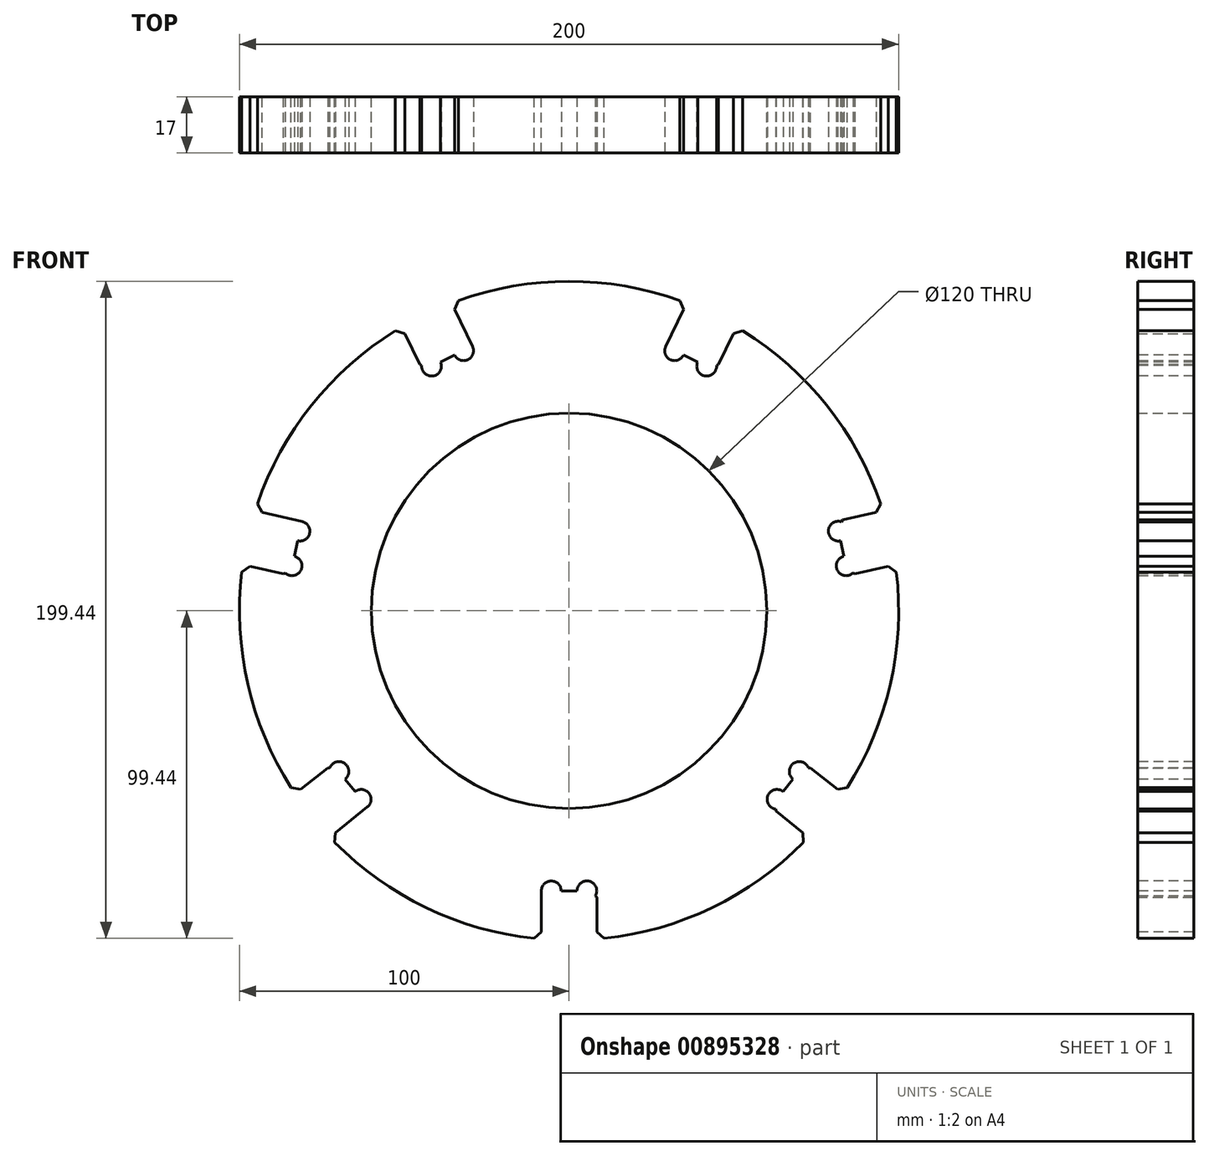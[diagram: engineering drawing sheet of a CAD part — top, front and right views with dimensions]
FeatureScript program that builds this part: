
annotation { "Feature Type Name" : "Feature", "Feature Type Description" : "" }
export const myFeature = defineFeature(function(context is Context, id is Id, definition is map)
    precondition{}
    {
        {
            var Q0;
            Q0=qCreatedBy(makeId("Front.planeOp"),FACE);
            var sketch = newSketch(context, id + "F0", { "sketchPlane" : qUnion([Q0])});
            skArc(sketch, "E0", {"start": v(8.4, -99.65) * mm, "mid": v(43.39, -90.1) * mm, "end": v(72.67, -68.7) * mm});
            skCircle(sketch, "E1", {"center": v(0, 0) * mm, "radius": 60 * mm});
            skLineSegment(sketch, "E2", {"start": v(0, 0) * mm, "end": v(0, -60) * mm});
            skLineSegment(sketch, "E3.0", {"start": v(-8.4, 0) * mm, "end": v(-8.4, -59.4) * mm});
            skLineSegment(sketch, "E4.0", {"start": v(8.4, 0) * mm, "end": v(8.4, -59.4) * mm});
            skLineSegment(sketch, "E5", {"start": v(0, -85) * mm, "end": v(8.4, -85) * mm});
            skLineSegment(sketch, "E6", {"start": v(8.4, -85) * mm, "end": v(-8.4, -85) * mm});
            skLineSegment(sketch, "E7.trimOffspring", {"start": v(-8.4, -85) * mm, "end": v(-8.4, -100) * mm});
            skLineSegment(sketch, "E8.trimOffspring", {"start": v(8.4, -85) * mm, "end": v(8.4, -100) * mm});
            skLineSegment(sketch, "E9.1.0", {"start": v(71.7, -46.43) * mm, "end": v(83.42, -55.78) * mm});
            skLineSegment(sketch, "E9.1.1", {"start": v(71.7, -46.43) * mm, "end": v(61.22, -59.56) * mm});
            skLineSegment(sketch, "E9.1.2", {"start": v(61.22, -59.56) * mm, "end": v(72.95, -68.92) * mm});
            skLineSegment(sketch, "E9.1.3", {"start": v(66.46, -53) * mm, "end": v(71.7, -46.43) * mm});
            skLineSegment(sketch, "E9.2.0", {"start": v(81, 27.1) * mm, "end": v(95.62, 30.44) * mm});
            skLineSegment(sketch, "E9.2.1", {"start": v(81, 27.1) * mm, "end": v(84.74, 10.72) * mm});
            skLineSegment(sketch, "E9.2.2", {"start": v(84.74, 10.72) * mm, "end": v(99.36, 14.06) * mm});
            skLineSegment(sketch, "E9.2.3", {"start": v(82.87, 18.91) * mm, "end": v(81, 27.1) * mm});
            skLineSegment(sketch, "E9.3.0", {"start": v(29.31, 80.23) * mm, "end": v(35.82, 93.74) * mm});
            skLineSegment(sketch, "E9.3.1", {"start": v(29.31, 80.23) * mm, "end": v(44.45, 72.94) * mm});
            skLineSegment(sketch, "E9.3.2", {"start": v(44.45, 72.94) * mm, "end": v(50.96, 86.45) * mm});
            skLineSegment(sketch, "E9.3.3", {"start": v(36.88, 76.58) * mm, "end": v(29.31, 80.23) * mm});
            skLineSegment(sketch, "E9.4.0", {"start": v(-44.45, 72.94) * mm, "end": v(-50.96, 86.45) * mm});
            skLineSegment(sketch, "E9.4.1", {"start": v(-44.45, 72.94) * mm, "end": v(-29.31, 80.23) * mm});
            skLineSegment(sketch, "E9.4.2", {"start": v(-29.31, 80.23) * mm, "end": v(-35.82, 93.74) * mm});
            skLineSegment(sketch, "E9.4.3", {"start": v(-36.88, 76.58) * mm, "end": v(-44.45, 72.94) * mm});
            skLineSegment(sketch, "E9.5.0", {"start": v(-84.74, 10.72) * mm, "end": v(-99.36, 14.06) * mm});
            skLineSegment(sketch, "E9.5.1", {"start": v(-84.74, 10.72) * mm, "end": v(-81, 27.1) * mm});
            skLineSegment(sketch, "E9.5.2", {"start": v(-81, 27.1) * mm, "end": v(-95.62, 30.44) * mm});
            skLineSegment(sketch, "E9.5.3", {"start": v(-82.87, 18.91) * mm, "end": v(-84.74, 10.72) * mm});
            skLineSegment(sketch, "E9.6.0", {"start": v(-61.22, -59.56) * mm, "end": v(-72.95, -68.92) * mm});
            skLineSegment(sketch, "E9.6.1", {"start": v(-61.22, -59.56) * mm, "end": v(-71.7, -46.43) * mm});
            skLineSegment(sketch, "E9.6.2", {"start": v(-71.7, -46.43) * mm, "end": v(-83.42, -55.78) * mm});
            skLineSegment(sketch, "E9.6.3", {"start": v(-66.46, -53) * mm, "end": v(-61.22, -59.56) * mm});
            skArc(sketch, "E10.trimOffspring", {"start": v(-99.02, 13.98) * mm, "mid": v(-99.9, -4.49) * mm, "end": v(-97.37, -22.8) * mm});
            skArc(sketch, "E11.trimOffspring", {"start": v(-92.17, -38.78) * mm, "mid": v(-88.06, -47.39) * mm, "end": v(-83.14, -55.56) * mm});
            skArc(sketch, "E12.trimOffspring", {"start": v(-72.67, -68.7) * mm, "mid": v(-43.39, -90.1) * mm, "end": v(-8.4, -99.65) * mm});
            skArc(sketch, "E13.trimOffspring", {"start": v(-99.02, 13.98) * mm, "mid": v(-97.5, -22.25) * mm, "end": v(-83.14, -55.56) * mm});
            skArc(sketch, "E14.trimOffspring", {"start": v(-50.8, 86.13) * mm, "mid": v(-78.18, 62.35) * mm, "end": v(-95.28, 30.36) * mm});
            skArc(sketch, "E15.trimOffspring", {"start": v(35.67, 93.42) * mm, "mid": v(0, 100) * mm, "end": v(-35.67, 93.42) * mm});
            skArc(sketch, "E16.trimOffspring", {"start": v(95.28, 30.36) * mm, "mid": v(78.18, 62.35) * mm, "end": v(50.8, 86.13) * mm});
            skArc(sketch, "E17.trimOffspring", {"start": v(83.14, -55.56) * mm, "mid": v(97.5, -22.25) * mm, "end": v(99.02, 13.98) * mm});
            skArc(sketch, "E18.trimOffspring", {"start": v(95.28, 30.36) * mm, "mid": v(86.13, 50.8) * mm, "end": v(72.67, 68.7) * mm});
            skArc(sketch, "E19.trimOffspring", {"start": v(-50.8, 86.13) * mm, "mid": v(-75.3, 65.8) * mm, "end": v(-92.17, 38.78) * mm});
            skSolve(sketch);
        }
        {
            var Q0;
            Q0 = qSketchRegion(id + "F0", true);
            extrude(context, id + "F1", {"entities" : qUnion([Q0]), "depth" : 17 * mm, "offsetDistance" : 25 * mm});
        }
        {
            var Q0;
            Q0 = qSketchRegion(id + "F0", true);
            extrude(context, id + "F2", {"entities" : qUnion([Q0]), "operationType" : NewBodyOperationType.ADD, "depth" : 17 * mm, "offsetDistance" : 25 * mm});
        }
        {
            var Q0;
            Q0=makeQuery(id+"F1.opExtrude","SWEPT_EDGE",EDGE,{"disambiguationData":[OSD([sQuery(id+"F0.wireOp",EDGE,"E9.4.0"),sQuery(id+"F0.wireOp",EDGE,"E19.trimOffspring")])]});
            var Q1;
            Q1=makeQuery(id+"F1.opExtrude","SWEPT_EDGE",EDGE,{"disambiguationData":[OSD([sQuery(id+"F0.wireOp",EDGE,"E9.4.2"),sQuery(id+"F0.wireOp",EDGE,"E15.trimOffspring")])]});
            var Q2;
            Q2=makeQuery(id+"F1.opExtrude","SWEPT_EDGE",EDGE,{"disambiguationData":[OSD([sQuery(id+"F0.wireOp",EDGE,"E9.3.0"),sQuery(id+"F0.wireOp",EDGE,"E15.trimOffspring")])]});
            var Q3;
            Q3=makeQuery(id+"F1.opExtrude","SWEPT_EDGE",EDGE,{"disambiguationData":[OSD([sQuery(id+"F0.wireOp",EDGE,"E9.3.2"),sQuery(id+"F0.wireOp",EDGE,"E16.trimOffspring")])]});
            var Q4;
            Q4=makeQuery(id+"F1.opExtrude","SWEPT_EDGE",EDGE,{"disambiguationData":[OSD([sQuery(id+"F0.wireOp",EDGE,"E9.2.0"),sQuery(id+"F0.wireOp",EDGE,"E16.trimOffspring")])]});
            var Q5;
            Q5=makeQuery(id+"F1.opExtrude","SWEPT_EDGE",EDGE,{"disambiguationData":[OSD([sQuery(id+"F0.wireOp",EDGE,"E9.2.2"),sQuery(id+"F0.wireOp",EDGE,"E17.trimOffspring")])]});
            var Q6;
            Q6=makeQuery(id+"F1.opExtrude","SWEPT_EDGE",EDGE,{"disambiguationData":[OSD([sQuery(id+"F0.wireOp",EDGE,"E9.1.0"),sQuery(id+"F0.wireOp",EDGE,"E17.trimOffspring")])]});
            var Q7;
            Q7=makeQuery(id+"F1.opExtrude","SWEPT_EDGE",EDGE,{"disambiguationData":[OSD([sQuery(id+"F0.wireOp",EDGE,"E9.1.2"),sQuery(id+"F0.wireOp",EDGE,"E0")])]});
            var Q8;
            Q8=makeQuery(id+"F1.opExtrude","SWEPT_EDGE",EDGE,{"disambiguationData":[OSD([sQuery(id+"F0.wireOp",EDGE,"E8.trimOffspring"),sQuery(id+"F0.wireOp",EDGE,"E0")])]});
            var Q9;
            Q9=makeQuery(id+"F1.opExtrude","SWEPT_EDGE",EDGE,{"disambiguationData":[OSD([sQuery(id+"F0.wireOp",EDGE,"E7.trimOffspring"),sQuery(id+"F0.wireOp",EDGE,"E12.trimOffspring")])]});
            var Q10;
            Q10=makeQuery(id+"F1.opExtrude","SWEPT_EDGE",EDGE,{"disambiguationData":[OSD([sQuery(id+"F0.wireOp",EDGE,"E9.6.0"),sQuery(id+"F0.wireOp",EDGE,"E12.trimOffspring")])]});
            var Q11;
            Q11=makeQuery(id+"F1.opExtrude","SWEPT_EDGE",EDGE,{"disambiguationData":[OSD([sQuery(id+"F0.wireOp",EDGE,"E9.6.2"),sQuery(id+"F0.wireOp",EDGE,"E13.trimOffspring")])]});
            var Q12;
            Q12=makeQuery(id+"F1.opExtrude","SWEPT_EDGE",EDGE,{"disambiguationData":[OSD([sQuery(id+"F0.wireOp",EDGE,"E9.5.2"),sQuery(id+"F0.wireOp",EDGE,"E14.trimOffspring")])]});
            var Q13;
            Q13=makeQuery(id+"F1.opExtrude","SWEPT_EDGE",EDGE,{"disambiguationData":[OSD([sQuery(id+"F0.wireOp",EDGE,"E9.5.0"),sQuery(id+"F0.wireOp",EDGE,"E13.trimOffspring")])]});
            chamfer(context, id + "F3", {"entities" : qUnion([Q0, Q1, Q2, Q3, Q4, Q5, Q6, Q7, Q8, Q9, Q10, Q11, Q12, Q13]), "width" : 2 * mm, "tangentPropagation" : true});
        }
        {
            var Q0;
            Q0=makeQuery(id+"F1.opExtrude","CAP_FACE",FACE,{"disambiguationData":[OSD([sQuery(id+"F0.wireOp",EDGE,"E1"),sQuery(id+"F0.wireOp",EDGE,"E6"),sQuery(id+"F0.wireOp",EDGE,"E7.trimOffspring"),sQuery(id+"F0.wireOp",EDGE,"E8.trimOffspring"),sQuery(id+"F0.wireOp",EDGE,"E9.1.0"),sQuery(id+"F0.wireOp",EDGE,"E9.1.1"),sQuery(id+"F0.wireOp",EDGE,"E9.1.2"),sQuery(id+"F0.wireOp",EDGE,"E9.1.3"),sQuery(id+"F0.wireOp",EDGE,"E9.2.0"),sQuery(id+"F0.wireOp",EDGE,"E9.2.1"),sQuery(id+"F0.wireOp",EDGE,"E9.2.2"),sQuery(id+"F0.wireOp",EDGE,"E9.2.3"),sQuery(id+"F0.wireOp",EDGE,"E9.3.0"),sQuery(id+"F0.wireOp",EDGE,"E9.3.1"),sQuery(id+"F0.wireOp",EDGE,"E9.3.2"),sQuery(id+"F0.wireOp",EDGE,"E9.3.3"),sQuery(id+"F0.wireOp",EDGE,"E9.4.0"),sQuery(id+"F0.wireOp",EDGE,"E9.4.1"),sQuery(id+"F0.wireOp",EDGE,"E9.4.2"),sQuery(id+"F0.wireOp",EDGE,"E9.4.3"),sQuery(id+"F0.wireOp",EDGE,"E9.5.0"),sQuery(id+"F0.wireOp",EDGE,"E9.5.1"),sQuery(id+"F0.wireOp",EDGE,"E9.5.2"),sQuery(id+"F0.wireOp",EDGE,"E9.5.3"),sQuery(id+"F0.wireOp",EDGE,"E9.6.0"),sQuery(id+"F0.wireOp",EDGE,"E9.6.1"),sQuery(id+"F0.wireOp",EDGE,"E9.6.2"),sQuery(id+"F0.wireOp",EDGE,"E9.6.3"),sQuery(id+"F0.wireOp",EDGE,"E13.trimOffspring"),sQuery(id+"F0.wireOp",EDGE,"E14.trimOffspring"),sQuery(id+"F0.wireOp",EDGE,"E12.trimOffspring"),sQuery(id+"F0.wireOp",EDGE,"E0"),sQuery(id+"F0.wireOp",EDGE,"E17.trimOffspring"),sQuery(id+"F0.wireOp",EDGE,"E16.trimOffspring"),sQuery(id+"F0.wireOp",EDGE,"E15.trimOffspring"),sQuery(id+"F0.wireOp",EDGE,"E19.trimOffspring")])],"isStart":false});
            var sketch = newSketch(context, id + "F4", { "sketchPlane" : qUnion([Q0])});
            skLineSegment(sketch, "E20", {"start": v(-44.45, 72.94) * mm, "end": v(-29.31, 80.23) * mm});
            skCircle(sketch, "E21", {"center": v(-41.75, 74.24) * mm, "radius": 3 * mm});
            skLineSegment(sketch, "E22", {"start": v(-36.88, 76.58) * mm, "end": v(-37.6, 78.08) * mm});
            skCircle(sketch, "E23.MirrorC", {"center": v(-32.01, 78.93) * mm, "radius": 3 * mm});
            skCircle(sketch, "E24.1.0", {"center": v(-84.07, 13.65) * mm, "radius": 3 * mm});
            skCircle(sketch, "E24.1.1", {"center": v(-81.67, 24.18) * mm, "radius": 3 * mm});
            skCircle(sketch, "E24.2.0", {"center": v(-63.09, -57.22) * mm, "radius": 3 * mm});
            skCircle(sketch, "E24.2.1", {"center": v(-69.82, -48.77) * mm, "radius": 3 * mm});
            skCircle(sketch, "E24.3.0", {"center": v(5.4, -85) * mm, "radius": 3 * mm});
            skCircle(sketch, "E24.3.1", {"center": v(-5.4, -85) * mm, "radius": 3 * mm});
            skCircle(sketch, "E24.4.0", {"center": v(69.82, -48.77) * mm, "radius": 3 * mm});
            skCircle(sketch, "E24.4.1", {"center": v(63.09, -57.22) * mm, "radius": 3 * mm});
            skCircle(sketch, "E24.5.0", {"center": v(81.67, 24.18) * mm, "radius": 3 * mm});
            skCircle(sketch, "E24.5.1", {"center": v(84.07, 13.65) * mm, "radius": 3 * mm});
            skCircle(sketch, "E24.6.0", {"center": v(32.01, 78.93) * mm, "radius": 3 * mm});
            skCircle(sketch, "E24.6.1", {"center": v(41.75, 74.24) * mm, "radius": 3 * mm});
            skPoint(sketch, "E24.center", {"position": v(0, 0) * mm});
            skSolve(sketch);
        }
        {
            var Q0;
            Q0 = qSketchRegion(id + "F4", true);
            extrude(context, id + "F5", {"entities" : qUnion([Q0]), "operationType" : NewBodyOperationType.REMOVE, "oppositeDirection" : true, "depth" : 25 * mm, "offsetDistance" : 25 * mm});
        }
    });
